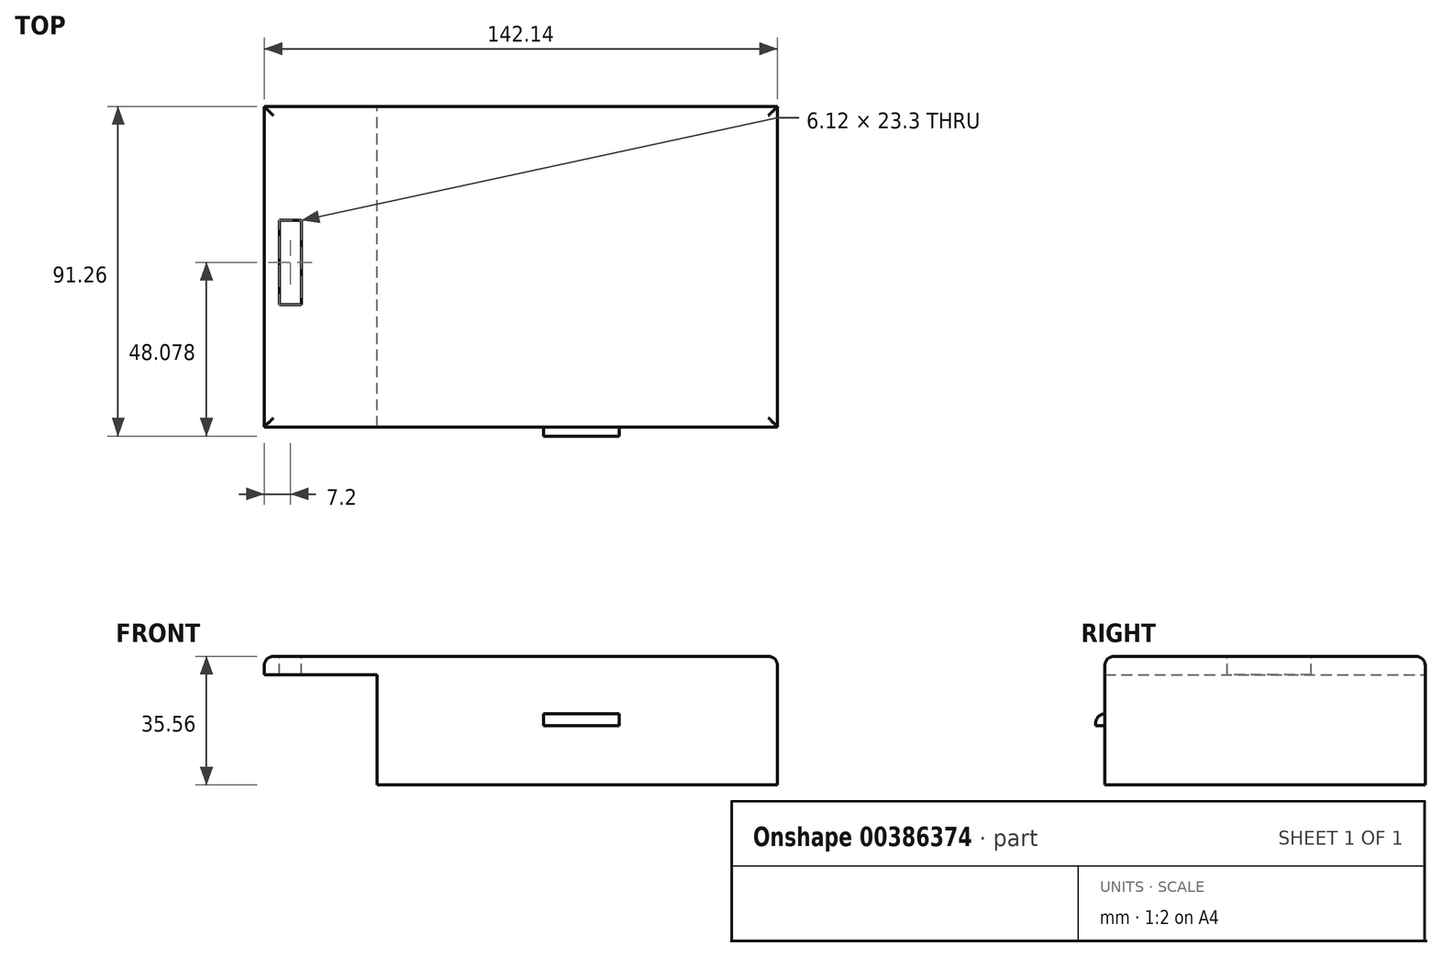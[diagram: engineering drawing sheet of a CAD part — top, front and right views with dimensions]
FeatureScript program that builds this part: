
annotation { "Feature Type Name" : "Feature", "Feature Type Description" : "" }
export const myFeature = defineFeature(function(context is Context, id is Id, definition is map)
    precondition{}
    {
        {
            var Q0;
            Q0=qCreatedBy(makeId("Top.planeOp"),FACE);
            var sketch = newSketch(context, id + "F0", { "sketchPlane" : qUnion([Q0])});
            skLineSegment(sketch, "E0.bottom", {"start": v(-54.36, 54.83) * mm, "end": v(87.78, 54.83) * mm});
            skLineSegment(sketch, "E0.top", {"start": v(-54.36, -33.89) * mm, "end": v(87.78, -33.89) * mm});
            skLineSegment(sketch, "E0.left", {"start": v(-54.36, 54.83) * mm, "end": v(-54.36, -33.89) * mm});
            skLineSegment(sketch, "E0.right", {"start": v(87.78, 54.83) * mm, "end": v(87.78, -33.89) * mm});
            skSolve(sketch);
        }
        {
            var Q0;
            Q0=makeQuery(id+"F0.imprint","IMPRINT",FACE,{"disambiguationData":[TD([[makeQuery(id+"F0.imprint","IMPRINT",EDGE,{"derivedFrom":sQuery(id+"F0.wireOp",EDGE,"E0.bottom")}),-1.0]])]});
            extrude(context, id + "F1", {"entities" : qUnion([Q0]), "depth" : 5.08 * mm});
        }
        {
            var Q0;
            Q0=makeQuery(id+"F1.opExtrude","CAP_FACE",FACE,{"disambiguationData":[OSD([sQuery(id+"F0.wireOp",EDGE,"E0.bottom"),sQuery(id+"F0.wireOp",EDGE,"E0.top"),sQuery(id+"F0.wireOp",EDGE,"E0.left"),sQuery(id+"F0.wireOp",EDGE,"E0.right")])],"isStart":false});
            var sketch = newSketch(context, id + "F2", { "sketchPlane" : qUnion([Q0])});
            skLineSegment(sketch, "E1.bottom", {"start": v(-50.22, 23.3) * mm, "end": v(-44.1, 23.3) * mm});
            skLineSegment(sketch, "E1.top", {"start": v(-50.22, 0) * mm, "end": v(-44.1, 0) * mm});
            skLineSegment(sketch, "E1.left", {"start": v(-50.22, 23.3) * mm, "end": v(-50.22, 0) * mm});
            skLineSegment(sketch, "E1.right", {"start": v(-44.1, 23.3) * mm, "end": v(-44.1, 0) * mm});
            skSolve(sketch);
        }
        {
            var Q0;
            Q0=makeQuery(id+"F2.imprint","IMPRINT",FACE,{"disambiguationData":[TD([[makeQuery(id+"F2.imprint","IMPRINT",EDGE,{"derivedFrom":sQuery(id+"F2.wireOp",EDGE,"E1.bottom")}),-1.0]])]});
            extrude(context, id + "F3", {"entities" : qUnion([Q0]), "operationType" : NewBodyOperationType.REMOVE, "oppositeDirection" : true, "depth" : 25.4 * mm});
        }
        {
            var Q0;
            Q0=makeQuery(id+"F1.opExtrude","CAP_FACE",FACE,{"disambiguationData":[OSD([sQuery(id+"F0.wireOp",EDGE,"E0.bottom"),sQuery(id+"F0.wireOp",EDGE,"E0.top"),sQuery(id+"F0.wireOp",EDGE,"E0.left"),sQuery(id+"F0.wireOp",EDGE,"E0.right")])],"isStart":true});
            var sketch = newSketch(context, id + "F4", { "sketchPlane" : qUnion([Q0])});
            skLineSegment(sketch, "E2.bottom", {"start": v(87.78, 33.89) * mm, "end": v(-23.16, 33.89) * mm});
            skLineSegment(sketch, "E2.top", {"start": v(87.78, -54.83) * mm, "end": v(-23.16, -54.83) * mm});
            skLineSegment(sketch, "E2.left", {"start": v(87.78, 33.89) * mm, "end": v(87.78, -54.83) * mm});
            skLineSegment(sketch, "E2.right", {"start": v(-23.16, 33.89) * mm, "end": v(-23.16, -54.83) * mm});
            skSolve(sketch);
        }
        {
            var Q0;
            Q0=makeQuery(id+"F4.imprint","IMPRINT",FACE,{"disambiguationData":[TD([[makeQuery(id+"F4.imprint","IMPRINT",EDGE,{"derivedFrom":sQuery(id+"F4.wireOp",EDGE,"E2.bottom")}),-1.0]])]});
            extrude(context, id + "F5", {"entities" : qUnion([Q0]), "operationType" : NewBodyOperationType.ADD, "depth" : 30.48 * mm});
        }
        {
            var Q0;
            Q0=makeQuery(id+"F5.boolean.opBoolean","MERGE",FACE,{"derivedFrom":[makeQuery(id+"F1.opExtrude","SWEPT_FACE",FACE,{"disambiguationData":[OSD([sQuery(id+"F0.wireOp",EDGE,"E0.top")])]}),makeQuery(id+"F5.opExtrude","SWEPT_FACE",FACE,{"disambiguationData":[OSD([sQuery(id+"F4.wireOp",EDGE,"E2.bottom")])]})]});
            var sketch = newSketch(context, id + "F6", { "sketchPlane" : qUnion([Q0])});
            skLineSegment(sketch, "E3.bottom", {"start": v(22.97, -10.82) * mm, "end": v(43.91, -10.82) * mm});
            skLineSegment(sketch, "E3.top", {"start": v(22.97, -14.12) * mm, "end": v(43.91, -14.12) * mm});
            skLineSegment(sketch, "E3.left", {"start": v(22.97, -10.82) * mm, "end": v(22.97, -14.12) * mm});
            skLineSegment(sketch, "E3.right", {"start": v(43.91, -10.82) * mm, "end": v(43.91, -14.12) * mm});
            skSolve(sketch);
        }
        {
            var Q0;
            Q0=makeQuery(id+"F6.imprint","IMPRINT",FACE,{"disambiguationData":[TD([[makeQuery(id+"F6.imprint","IMPRINT",EDGE,{"derivedFrom":sQuery(id+"F6.wireOp",EDGE,"E3.bottom")}),-1.0]])]});
            extrude(context, id + "F7", {"entities" : qUnion([Q0]), "operationType" : NewBodyOperationType.ADD, "depth" : 2.54 * mm});
        }
        {
            var Q0;
            Q0=makeQuery(id+"F1.opExtrude","CAP_EDGE",EDGE,{"disambiguationData":[OSD([sQuery(id+"F0.wireOp",EDGE,"E0.top")])],"isStart":false});
            var Q1;
            Q1=makeQuery(id+"F1.opExtrude","CAP_EDGE",EDGE,{"disambiguationData":[OSD([sQuery(id+"F0.wireOp",EDGE,"E0.left")])],"isStart":false});
            var Q2;
            Q2=makeQuery(id+"F1.opExtrude","CAP_EDGE",EDGE,{"disambiguationData":[OSD([sQuery(id+"F0.wireOp",EDGE,"E0.bottom")])],"isStart":false});
            var Q3;
            Q3=makeQuery(id+"F1.opExtrude","CAP_EDGE",EDGE,{"disambiguationData":[OSD([sQuery(id+"F0.wireOp",EDGE,"E0.right")])],"isStart":false});
            fillet(context, id + "F8", {"entities" : qUnion([Q0, Q1, Q2, Q3]), "radius" : 2.54 * mm, "tangentPropagation" : true, "allowEdgeOverflow" : false});
        }
        {
            var Q0;
            Q0=makeQuery(id+"F7.opExtrude","CAP_EDGE",EDGE,{"disambiguationData":[OSD([sQuery(id+"F6.wireOp",EDGE,"E3.bottom")])],"isStart":false});
            fillet(context, id + "F9", {"entities" : qUnion([Q0]), "radius" : 2.54 * mm, "tangentPropagation" : true, "allowEdgeOverflow" : false});
        }
    });
